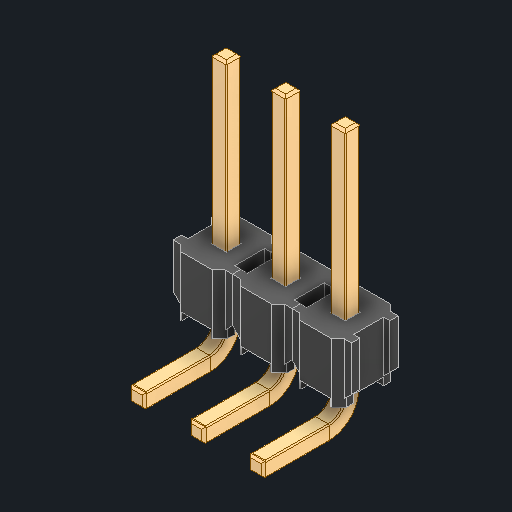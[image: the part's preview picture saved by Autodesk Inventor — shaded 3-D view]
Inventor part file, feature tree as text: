
AUTODESK INVENTOR PART (.ipt)
format: ipt  version: 2024 (Build 280153000, 153)  size: 262,144 bytes
history: native  units: mm
features: other x11, fillet x1
ambient origin geometry x8: Origin, YZ Plane, XZ Plane, XY Plane, X Axis, Y Axis, Z Axis, Center Point
bodies: Body1 (feature_tree), Body2 (feature_tree), Body3 (feature_tree), Body4 (feature_tree), Body5 (feature_tree), Body6 (feature_tree)
feature tree (12):
  other  "Těleso1"
  other  "Těleso2"
  other  "Těleso3"
  other  "Těleso4"
  other  "Těleso5"
  other  "Těleso6"
  other  "Cortar-Extruir6"
  fillet  "Redondeo6"  [1 undecoded]
  other  "MatrizL1[1]"
  other  "MatrizL1[2]"
  other  "MatrizL1[3]"
  other  "MatrizL1[4]"
note: 1 required parameter value undecoded (feature->parameter linkage not recoverable at this tier; creation-order binding heuristic only, values carry confidence <= 0.55)
